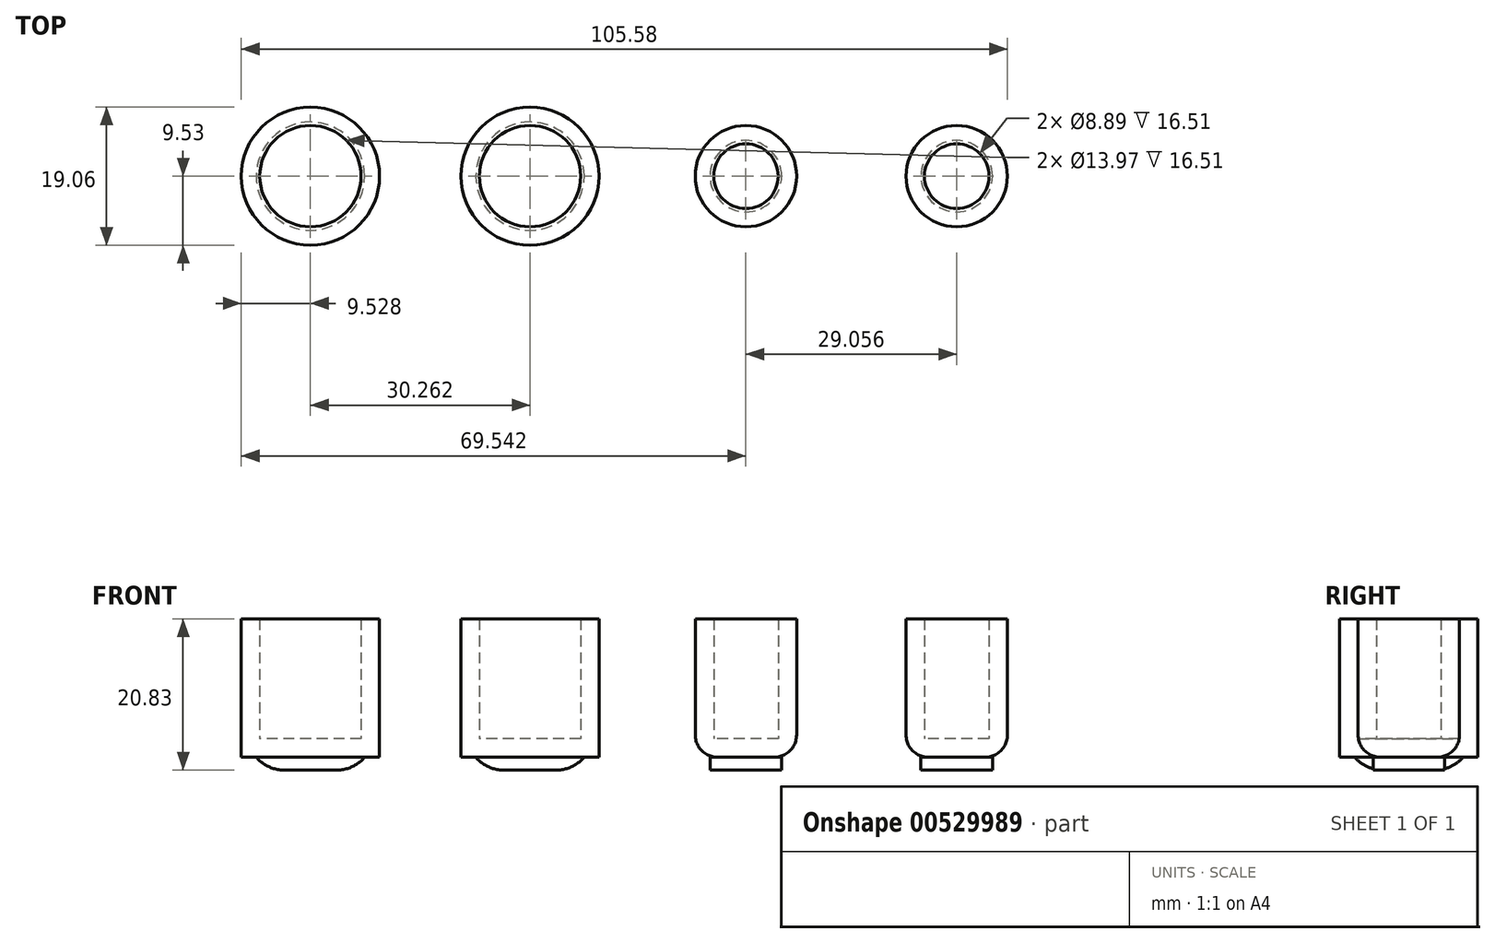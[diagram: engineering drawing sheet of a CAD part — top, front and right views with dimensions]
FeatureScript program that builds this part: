
annotation { "Feature Type Name" : "Feature", "Feature Type Description" : "" }
export const myFeature = defineFeature(function(context is Context, id is Id, definition is map)
    precondition{}
    {
        {
            var Q0;
            Q0=qCreatedBy(makeId("Top.planeOp"),FACE);
            var sketch = newSketch(context, id + "F0", { "sketchPlane" : qUnion([Q0])});
            skCircle(sketch, "E0", {"center": v(0, 0) * mm, "radius": 9.53 * mm});
            skSolve(sketch);
        }
        {
            var Q0;
            Q0 = qSketchRegion(id + "F0", true);
            extrude(context, id + "F1", {"entities" : qUnion([Q0]), "depth" : 19.05 * mm, "offsetDistance" : 25.4 * mm});
        }
        {
            var Q0;
            Q0=makeQuery(id+"F1.opExtrude","CAP_FACE",FACE,{"disambiguationData":[OSD([sQuery(id+"F0.wireOp",EDGE,"E0")])],"isStart":false});
            shell(context, id + "F2", {"entities" : qUnion([Q0]), "thickness" : 2.54 * mm});
        }
        {
            var Q0;
            Q0=makeQuery(id+"F1.opExtrude","CAP_FACE",FACE,{"disambiguationData":[OSD([sQuery(id+"F0.wireOp",EDGE,"E0")])],"isStart":true});
            var sketch = newSketch(context, id + "F3", { "sketchPlane" : qUnion([Q0])});
            skCircle(sketch, "E1", {"center": v(0, 0) * mm, "radius": 7.47 * mm});
            skSolve(sketch);
        }
        {
            var Q0;
            Q0 = qSketchRegion(id + "F3", true);
            extrude(context, id + "F4", {"entities" : qUnion([Q0]), "operationType" : NewBodyOperationType.ADD, "depth" : 1.78 * mm, "offsetDistance" : 25.4 * mm});
        }
        {
            var Q0;
            Q0=makeQuery(id+"F4.opExtrude","CAP_EDGE",EDGE,{"disambiguationData":[OSD([sQuery(id+"F3.wireOp",EDGE,"E1")])],"isStart":false});
            fillet(context, id + "F5", {"entities" : qUnion([Q0]), "radius" : 5.08 * mm, "tangentPropagation" : true, "allowEdgeOverflow" : false});
        }
        {
            var Q0;
            Q0=qCreatedBy(makeId("Top.planeOp"),FACE);
            var sketch = newSketch(context, id + "F6", { "sketchPlane" : qUnion([Q0])});
            skCircle(sketch, "E2", {"center": v(-30.26, 0) * mm, "radius": 9.53 * mm});
            skSolve(sketch);
        }
        {
            var Q0;
            Q0=makeQuery(id+"F6.imprint","IMPRINT",FACE,{"disambiguationData":[TD([[makeQuery(id+"F6.imprint","IMPRINT",EDGE,{"derivedFrom":sQuery(id+"F6.wireOp",EDGE,"E2")}),1.0]])]});
            extrude(context, id + "F7", {"entities" : qUnion([Q0]), "depth" : 19.05 * mm, "offsetDistance" : 25.4 * mm});
        }
        {
            var Q0;
            Q0=makeQuery(id+"F7.opExtrude","CAP_FACE",FACE,{"disambiguationData":[OSD([sQuery(id+"F6.wireOp",EDGE,"E2")])],"isStart":false});
            shell(context, id + "F8", {"entities" : qUnion([Q0]), "thickness" : 2.54 * mm});
        }
        {
            var Q0;
            Q0=makeQuery(id+"F7.opExtrude","CAP_FACE",FACE,{"disambiguationData":[OSD([sQuery(id+"F6.wireOp",EDGE,"E2")])],"isStart":true});
            var sketch = newSketch(context, id + "F9", { "sketchPlane" : qUnion([Q0])});
            skCircle(sketch, "E3", {"center": v(-30.26, 0) * mm, "radius": 7.47 * mm});
            skSolve(sketch);
        }
        {
            var Q0;
            Q0=makeQuery(id+"F9.imprint","IMPRINT",FACE,{"disambiguationData":[TD([[makeQuery(id+"F9.imprint","IMPRINT",EDGE,{"derivedFrom":sQuery(id+"F9.wireOp",EDGE,"E3")}),1.0]])]});
            extrude(context, id + "F10", {"entities" : qUnion([Q0]), "operationType" : NewBodyOperationType.ADD, "depth" : 1.78 * mm, "offsetDistance" : 25.4 * mm});
        }
        {
            var Q0;
            Q0=makeQuery(id+"F10.opExtrude","CAP_FACE",FACE,{"disambiguationData":[OSD([sQuery(id+"F9.wireOp",EDGE,"E3")])],"isStart":false});
            fillet(context, id + "F11", {"entities" : qUnion([Q0]), "radius" : 5.08 * mm, "tangentPropagation" : true, "allowEdgeOverflow" : false});
        }
        {
            var Q0;
            Q0=qCreatedBy(makeId("Top.planeOp"),FACE);
            var sketch = newSketch(context, id + "F12", { "sketchPlane" : qUnion([Q0])});
            skCircle(sketch, "E4", {"center": v(29.75, 0) * mm, "radius": 6.99 * mm});
            skCircle(sketch, "E5", {"center": v(58.8, 0) * mm, "radius": 6.99 * mm});
            skSolve(sketch);
        }
        {
            var Q0;
            Q0=makeQuery(id+"F12.imprint","IMPRINT",FACE,{"disambiguationData":[TD([[makeQuery(id+"F12.imprint","IMPRINT",EDGE,{"derivedFrom":sQuery(id+"F12.wireOp",EDGE,"E4")}),1.0]])]});
            var Q1;
            Q1=makeQuery(id+"F12.imprint","IMPRINT",FACE,{"disambiguationData":[TD([[makeQuery(id+"F12.imprint","IMPRINT",EDGE,{"derivedFrom":sQuery(id+"F12.wireOp",EDGE,"E5")}),1.0]])]});
            extrude(context, id + "F13", {"entities" : qUnion([Q0, Q1]), "depth" : 19.05 * mm, "offsetDistance" : 25.4 * mm});
        }
        {
            var Q0;
            Q0=makeQuery(id+"F13.opExtrude","CAP_FACE",FACE,{"disambiguationData":[OSD([sQuery(id+"F12.wireOp",EDGE,"E5")])],"isStart":false});
            var Q1;
            Q1=makeQuery(id+"F13.opExtrude","CAP_FACE",FACE,{"disambiguationData":[OSD([sQuery(id+"F12.wireOp",EDGE,"E4")])],"isStart":false});
            shell(context, id + "F14", {"entities" : qUnion([Q0, Q1]), "thickness" : 2.54 * mm});
        }
        {
            var Q0;
            Q0=makeQuery(id+"F13.opExtrude","CAP_FACE",FACE,{"disambiguationData":[OSD([sQuery(id+"F12.wireOp",EDGE,"E4")])],"isStart":true});
            var sketch = newSketch(context, id + "F15", { "sketchPlane" : qUnion([Q0])});
            skCircle(sketch, "E6", {"center": v(29.75, 0) * mm, "radius": 4.93 * mm});
            skSolve(sketch);
        }
        {
            var Q0;
            Q0=makeQuery(id+"F13.opExtrude","CAP_FACE",FACE,{"disambiguationData":[OSD([sQuery(id+"F12.wireOp",EDGE,"E5")])],"isStart":true});
            var sketch = newSketch(context, id + "F16", { "sketchPlane" : qUnion([Q0])});
            skCircle(sketch, "E7", {"center": v(58.8, 0) * mm, "radius": 4.93 * mm});
            skSolve(sketch);
        }
        {
            var Q0;
            Q0=makeQuery(id+"F15.imprint","IMPRINT",FACE,{"disambiguationData":[TD([[makeQuery(id+"F15.imprint","IMPRINT",EDGE,{"derivedFrom":sQuery(id+"F15.wireOp",EDGE,"E6")}),1.0]])]});
            var Q1;
            Q1=makeQuery(id+"F16.imprint","IMPRINT",FACE,{"disambiguationData":[TD([[makeQuery(id+"F16.imprint","IMPRINT",EDGE,{"derivedFrom":sQuery(id+"F16.wireOp",EDGE,"E7")}),1.0]])]});
            extrude(context, id + "F17", {"entities" : qUnion([Q0, Q1]), "depth" : 1.78 * mm, "offsetDistance" : 25.4 * mm});
        }
        {
            var Q0;
            Q0=makeQuery(id+"F13.opExtrude","CAP_EDGE",EDGE,{"disambiguationData":[OSD([sQuery(id+"F12.wireOp",EDGE,"E5")])],"isStart":true});
            fillet(context, id + "F18", {"entities" : qUnion([Q0]), "radius" : 3.07 * mm, "tangentPropagation" : true, "allowEdgeOverflow" : false});
        }
        {
            var Q0;
            Q0=makeQuery(id+"F13.opExtrude","CAP_EDGE",EDGE,{"disambiguationData":[OSD([sQuery(id+"F12.wireOp",EDGE,"E4")])],"isStart":true});
            fillet(context, id + "F19", {"entities" : qUnion([Q0]), "radius" : 3.07 * mm, "tangentPropagation" : true, "allowEdgeOverflow" : false});
        }
    });
